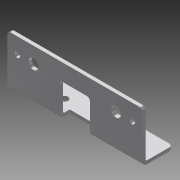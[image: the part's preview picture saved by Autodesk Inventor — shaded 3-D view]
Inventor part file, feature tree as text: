
AUTODESK INVENTOR PART (.ipt)
format: ipt  version: 2013 (Build 170138000, 138)  size: 270,848 bytes
history: native  units: in
note: dims shown in document units (in); Inventor stores cm internally (conversion verified against a paired STEP export)
features: other x7, sketch x6, sheet_metal_op x4, reference x3, chamfer x2
ambient origin geometry x8: Origin, YZ Plane, XZ Plane, XY Plane, X Axis, Y Axis, Z Axis, Center Point
bodies: Solid1 (feature_tree)
feature tree (22):
  sheet_metal_op  "Face1"
  sheet_metal_op  "Flange1"
  chamfer  "Corner Round1"
  chamfer  "Corner Round2"
  sketch  "Sketch1"  dims[d0=5.0in]
  other  "Plate1"
  sketch  "Sketch2"  dims[d1=1.125in]
  other  "Plate2"
  sheet_metal_op  "Bend1"
  sheet_metal_op  "Corner1"
  sketch  "Sketch3"  dims[d3=0.125in]
  sketch  "Sketch4"  dims[d4=0.125in]
  sketch  "Sketch5"  dims[d5=0.0625in]
  sketch  "Sketch6"  dims[d6=0.25in d7=0.125in d8=1.875in d9=90.0deg d10=0.05in d11=0.5in d12=0.125in d13=0.125in d18=1.125in d20=0.375in d21=0.0in d22=0.625in d23=0.26in d24=0.26in d25=2.0in d26=1.0in d27=0.125in d28=0.0in d29=0.125in d30=0.125in d31=0.0in d32=0.125in d33=0.0in d34=0.125in d35=0.375in d36=0.375in d37=1.25in d2=0.25in]
  reference  "Reference7"
  reference  "Reference14"
  reference  "Reference15"
  other  "Cut1"
  other  "Cut2"
  other  "Cut3"
  other  "Cut4"
  other  "Definition1"
